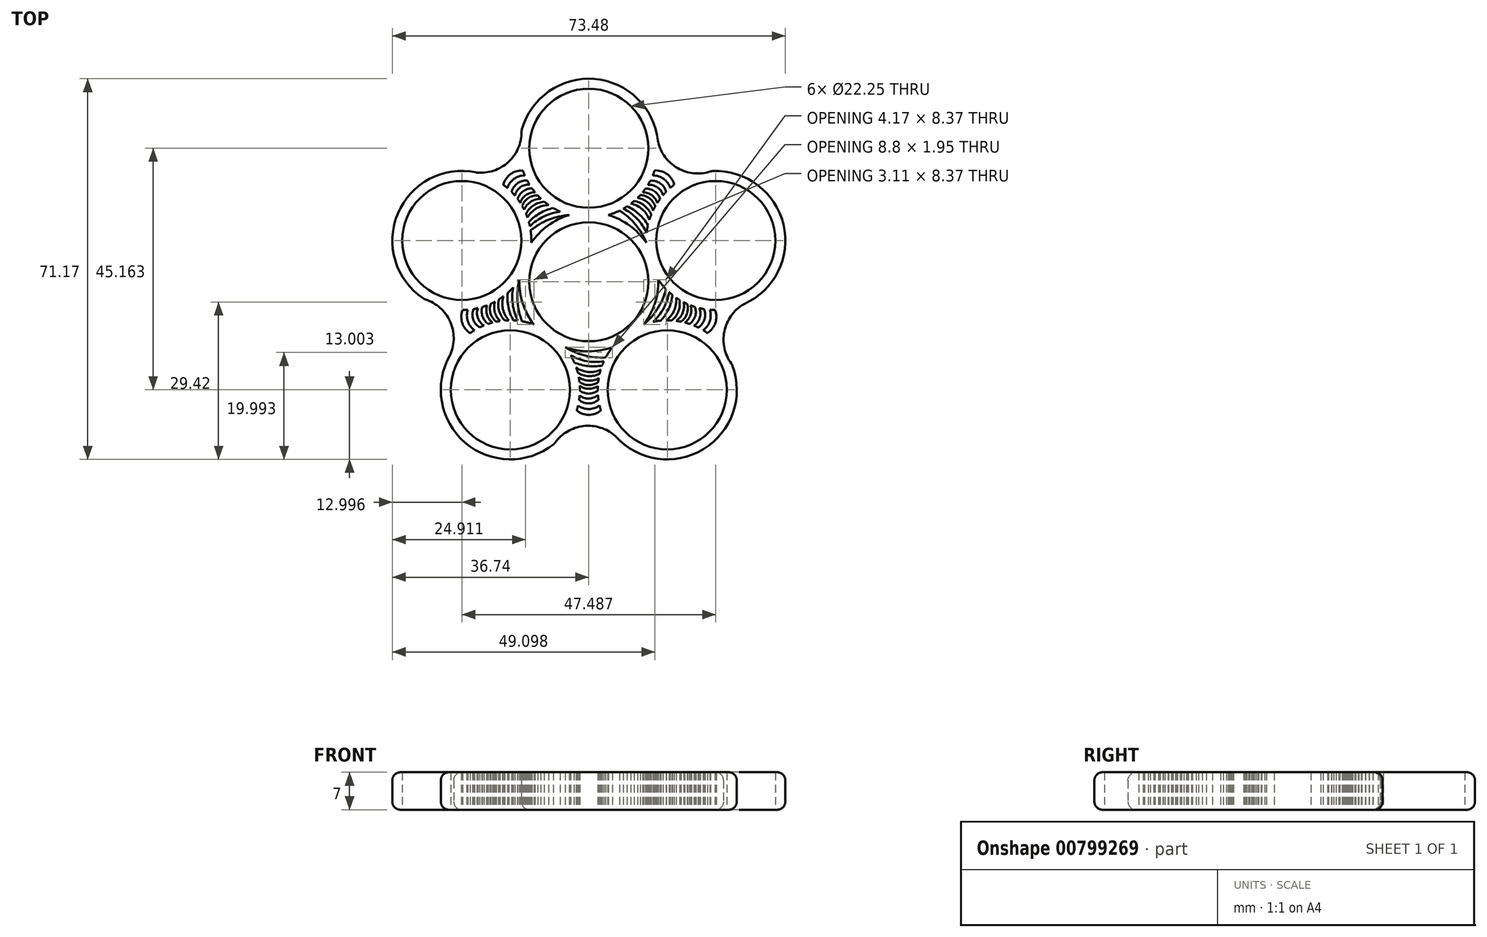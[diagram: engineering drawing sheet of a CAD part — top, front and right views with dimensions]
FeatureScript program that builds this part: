
annotation { "Feature Type Name" : "Feature", "Feature Type Description" : "" }
export const myFeature = defineFeature(function(context is Context, id is Id, definition is map)
    precondition{}
    {
        {
            var Q0;
            Q0=qCreatedBy(makeId("Top.planeOp"),FACE);
            var sketch = newSketch(context, id + "F0", { "sketchPlane" : qUnion([Q0])});
            skCircle(sketch, "E0", {"center": v(0, 0) * mm, "radius": 11.12 * mm});
            skCircle(sketch, "E1", {"center": v(0, 0) * mm, "radius": 13 * mm});
            skCircle(sketch, "E2", {"center": v(0, 24.97) * mm, "radius": 11.12 * mm});
            skCircle(sketch, "E3", {"center": v(0, 24.97) * mm, "radius": 13 * mm});
            skCircle(sketch, "E4.1.0", {"center": v(-23.74, 7.71) * mm, "radius": 11.12 * mm});
            skCircle(sketch, "E4.1.1", {"center": v(-23.74, 7.71) * mm, "radius": 13 * mm});
            skCircle(sketch, "E4.2.0", {"center": v(-14.67, -20.2) * mm, "radius": 11.12 * mm});
            skCircle(sketch, "E4.2.1", {"center": v(-14.67, -20.2) * mm, "radius": 13 * mm});
            skCircle(sketch, "E4.3.0", {"center": v(14.67, -20.2) * mm, "radius": 11.12 * mm});
            skCircle(sketch, "E4.3.1", {"center": v(14.67, -20.2) * mm, "radius": 13 * mm});
            skCircle(sketch, "E4.4.0", {"center": v(23.74, 7.71) * mm, "radius": 11.12 * mm});
            skCircle(sketch, "E4.4.1", {"center": v(23.74, 7.71) * mm, "radius": 13 * mm});
            skArc(sketch, "E5", {"start": v(-20.98, 20.42) * mm, "mid": v(-15.02, 22.43) * mm, "end": v(-12.58, 28.24) * mm});
            skArc(sketch, "E6.1.0", {"start": v(-25.9, -13.65) * mm, "mid": v(-25.97, -7.35) * mm, "end": v(-30.74, -3.24) * mm});
            skArc(sketch, "E6.2.0", {"start": v(4.98, -28.85) * mm, "mid": v(-1.04, -26.97) * mm, "end": v(-6.42, -30.24) * mm});
            skArc(sketch, "E6.3.0", {"start": v(28.98, -4.18) * mm, "mid": v(25.33, -9.32) * mm, "end": v(26.78, -15.45) * mm});
            skArc(sketch, "E6.4.0", {"start": v(12.93, 26.27) * mm, "mid": v(16.7, 21.21) * mm, "end": v(22.97, 20.7) * mm});
            skArc(sketch, "E7", {"start": v(15.97, 18.14) * mm, "mid": v(14.63, 20.14) * mm, "end": v(12.32, 20.81) * mm});
            skArc(sketch, "E8", {"start": v(15.22, 17.53) * mm, "mid": v(13.99, 19.25) * mm, "end": v(11.97, 19.89) * mm});
            skArc(sketch, "E9", {"start": v(14.44, 16.8) * mm, "mid": v(13.36, 18.4) * mm, "end": v(11.5, 18.9) * mm});
            skArc(sketch, "E10", {"start": v(13.88, 16.18) * mm, "mid": v(12.82, 17.66) * mm, "end": v(11.06, 18.14) * mm});
            skArc(sketch, "E11", {"start": v(13.33, 15.5) * mm, "mid": v(12.29, 16.92) * mm, "end": v(10.6, 17.44) * mm});
            skArc(sketch, "E12", {"start": v(12.8, 14.73) * mm, "mid": v(11.77, 16.19) * mm, "end": v(10.07, 16.75) * mm});
            skArc(sketch, "E13", {"start": v(12.42, 14.1) * mm, "mid": v(11.36, 15.6) * mm, "end": v(9.63, 16.23) * mm});
            skArc(sketch, "E14", {"start": v(12.01, 13.32) * mm, "mid": v(10.9, 14.93) * mm, "end": v(9.1, 15.68) * mm});
            skArc(sketch, "E15", {"start": v(11.67, 12.54) * mm, "mid": v(10.4, 14.24) * mm, "end": v(8.46, 15.1) * mm});
            skArc(sketch, "E16", {"start": v(11.33, 11.57) * mm, "mid": v(10, 13.56) * mm, "end": v(7.87, 14.62) * mm});
            skArc(sketch, "E17", {"start": v(11.06, 10.58) * mm, "mid": v(9.39, 12.65) * mm, "end": v(7.17, 14.12) * mm});
            skArc(sketch, "E18", {"start": v(10.82, 9.14) * mm, "mid": v(9.02, 11.78) * mm, "end": v(6.47, 13.69) * mm});
            skArc(sketch, "E19", {"start": v(10.75, 7.31) * mm, "mid": v(8.73, 10.7) * mm, "end": v(5.76, 13.31) * mm});
            skArc(sketch, "E20.1.0", {"start": v(-12.31, 20.8) * mm, "mid": v(-14.63, 20.14) * mm, "end": v(-15.99, 18.15) * mm});
            skArc(sketch, "E20.1.1", {"start": v(-11.97, 19.9) * mm, "mid": v(-13.99, 19.25) * mm, "end": v(-15.22, 17.53) * mm});
            skArc(sketch, "E20.1.2", {"start": v(-11.51, 18.93) * mm, "mid": v(-13.37, 18.4) * mm, "end": v(-14.42, 16.78) * mm});
            skArc(sketch, "E20.1.3", {"start": v(-11.1, 18.2) * mm, "mid": v(-12.84, 17.65) * mm, "end": v(-13.83, 16.12) * mm});
            skArc(sketch, "E20.1.4", {"start": v(-10.62, 17.47) * mm, "mid": v(-12.3, 16.91) * mm, "end": v(-13.31, 15.47) * mm});
            skArc(sketch, "E20.1.5", {"start": v(-10.05, 16.72) * mm, "mid": v(-11.76, 16.2) * mm, "end": v(-12.81, 14.75) * mm});
            skArc(sketch, "E20.1.6", {"start": v(-9.58, 16.18) * mm, "mid": v(-11.33, 15.63) * mm, "end": v(-12.46, 14.17) * mm});
            skArc(sketch, "E20.1.7", {"start": v(-8.95, 15.54) * mm, "mid": v(-10.83, 14.98) * mm, "end": v(-12.1, 13.5) * mm});
            skArc(sketch, "E20.1.8", {"start": v(-8.32, 14.98) * mm, "mid": v(-10.33, 14.3) * mm, "end": v(-11.74, 12.7) * mm});
            skArc(sketch, "E20.1.9", {"start": v(-7.5, 14.35) * mm, "mid": v(-9.8, 13.7) * mm, "end": v(-11.47, 12) * mm});
            skArc(sketch, "E20.1.10", {"start": v(-6.65, 13.8) * mm, "mid": v(-9.13, 12.84) * mm, "end": v(-11.22, 11.19) * mm});
            skArc(sketch, "E20.1.11", {"start": v(-5.35, 13.12) * mm, "mid": v(-8.41, 12.22) * mm, "end": v(-11.02, 10.38) * mm});
            skArc(sketch, "E20.1.12", {"start": v(-3.63, 12.48) * mm, "mid": v(-7.48, 11.61) * mm, "end": v(-10.88, 9.6) * mm});
            skArc(sketch, "E20.2.0", {"start": v(-23.58, -5.28) * mm, "mid": v(-23.67, -7.7) * mm, "end": v(-22.2, -9.6) * mm});
            skArc(sketch, "E20.2.1", {"start": v(-22.62, -5.24) * mm, "mid": v(-22.63, -7.35) * mm, "end": v(-21.37, -9.06) * mm});
            skArc(sketch, "E20.2.2", {"start": v(-21.56, -5.1) * mm, "mid": v(-21.63, -7.03) * mm, "end": v(-20.41, -8.53) * mm});
            skArc(sketch, "E20.2.3", {"start": v(-20.74, -4.93) * mm, "mid": v(-20.75, -6.75) * mm, "end": v(-19.6, -8.17) * mm});
            skArc(sketch, "E20.2.4", {"start": v(-19.9, -4.7) * mm, "mid": v(-19.88, -6.47) * mm, "end": v(-18.83, -7.88) * mm});
            skArc(sketch, "E20.2.5", {"start": v(-19, -4.4) * mm, "mid": v(-19.04, -6.18) * mm, "end": v(-18, -7.63) * mm});
            skArc(sketch, "E20.2.6", {"start": v(-18.34, -4.11) * mm, "mid": v(-18.36, -5.95) * mm, "end": v(-17.33, -7.47) * mm});
            skArc(sketch, "E20.2.7", {"start": v(-17.55, -3.71) * mm, "mid": v(-17.6, -5.67) * mm, "end": v(-16.58, -7.34) * mm});
            skArc(sketch, "E20.2.8", {"start": v(-16.81, -3.28) * mm, "mid": v(-16.79, -5.4) * mm, "end": v(-15.71, -7.24) * mm});
            skArc(sketch, "E20.2.9", {"start": v(-15.96, -2.7) * mm, "mid": v(-16.06, -5.08) * mm, "end": v(-14.96, -7.2) * mm});
            skArc(sketch, "E20.2.10", {"start": v(-15.17, -2.06) * mm, "mid": v(-15.03, -4.72) * mm, "end": v(-14.1, -7.21) * mm});
            skArc(sketch, "E20.2.11", {"start": v(-14.13, -1.03) * mm, "mid": v(-14.22, -4.22) * mm, "end": v(-13.28, -7.27) * mm});
            skArc(sketch, "E20.2.12", {"start": v(-13, 0.4) * mm, "mid": v(-13.36, -3.53) * mm, "end": v(-12.49, -7.38) * mm});
            skArc(sketch, "E20.3.0", {"start": v(-2.26, -24.06) * mm, "mid": v(0, -24.9) * mm, "end": v(2.27, -24.08) * mm});
            skArc(sketch, "E20.3.1", {"start": v(-2.01, -23.13) * mm, "mid": v(0, -23.8) * mm, "end": v(2, -23.12) * mm});
            skArc(sketch, "E20.3.2", {"start": v(-1.81, -22.08) * mm, "mid": v(0, -22.74) * mm, "end": v(1.8, -22.05) * mm});
            skArc(sketch, "E20.3.3", {"start": v(-1.72, -21.25) * mm, "mid": v(0.01, -21.83) * mm, "end": v(1.71, -21.17) * mm});
            skArc(sketch, "E20.3.4", {"start": v(-1.68, -20.38) * mm, "mid": v(0, -20.9) * mm, "end": v(1.68, -20.34) * mm});
            skArc(sketch, "E20.3.5", {"start": v(-1.7, -19.44) * mm, "mid": v(0, -20.02) * mm, "end": v(1.7, -19.47) * mm});
            skArc(sketch, "E20.3.6", {"start": v(-1.76, -18.72) * mm, "mid": v(-0.02, -19.3) * mm, "end": v(1.75, -18.79) * mm});
            skArc(sketch, "E20.3.7", {"start": v(-1.9, -17.84) * mm, "mid": v(-0.05, -18.49) * mm, "end": v(1.86, -18.03) * mm});
            skArc(sketch, "E20.3.8", {"start": v(-2.07, -17) * mm, "mid": v(-0.04, -17.64) * mm, "end": v(2.03, -17.18) * mm});
            skArc(sketch, "E20.3.9", {"start": v(-2.37, -16.02) * mm, "mid": v(-0.13, -16.85) * mm, "end": v(2.23, -16.45) * mm});
            skArc(sketch, "E20.3.10", {"start": v(-2.73, -15.07) * mm, "mid": v(-0.16, -15.75) * mm, "end": v(2.5, -15.64) * mm});
            skArc(sketch, "E20.3.11", {"start": v(-3.38, -13.75) * mm, "mid": v(-0.38, -14.83) * mm, "end": v(2.81, -14.88) * mm});
            skArc(sketch, "E20.3.12", {"start": v(-4.4, -12.23) * mm, "mid": v(-0.77, -13.8) * mm, "end": v(3.16, -14.16) * mm});
            skArc(sketch, "E20.4.0", {"start": v(22.18, -9.59) * mm, "mid": v(23.67, -7.7) * mm, "end": v(23.6, -5.28) * mm});
            skArc(sketch, "E20.4.1", {"start": v(21.38, -9.06) * mm, "mid": v(22.63, -7.35) * mm, "end": v(22.61, -5.24) * mm});
            skArc(sketch, "E20.4.2", {"start": v(20.44, -8.55) * mm, "mid": v(21.63, -7.02) * mm, "end": v(21.53, -5.1) * mm});
            skArc(sketch, "E20.4.3", {"start": v(19.68, -8.2) * mm, "mid": v(20.76, -6.73) * mm, "end": v(20.67, -4.92) * mm});
            skArc(sketch, "E20.4.4", {"start": v(18.86, -7.89) * mm, "mid": v(19.89, -6.46) * mm, "end": v(19.86, -4.7) * mm});
            skArc(sketch, "E20.4.5", {"start": v(17.96, -7.62) * mm, "mid": v(19.03, -6.2) * mm, "end": v(19.04, -4.4) * mm});
            skArc(sketch, "E20.4.6", {"start": v(17.26, -7.46) * mm, "mid": v(18.35, -5.98) * mm, "end": v(18.41, -4.14) * mm});
            skArc(sketch, "E20.4.7", {"start": v(16.38, -7.3) * mm, "mid": v(17.57, -5.76) * mm, "end": v(17.73, -3.8) * mm});
            skArc(sketch, "E20.4.8", {"start": v(15.53, -7.23) * mm, "mid": v(16.76, -5.5) * mm, "end": v(16.97, -3.38) * mm});
            skArc(sketch, "E20.4.9", {"start": v(14.5, -7.2) * mm, "mid": v(15.98, -5.33) * mm, "end": v(16.33, -2.97) * mm});
            skArc(sketch, "E20.4.10", {"start": v(13.49, -7.25) * mm, "mid": v(14.93, -5.02) * mm, "end": v(15.65, -2.46) * mm});
            skArc(sketch, "E20.4.11", {"start": v(12.04, -7.47) * mm, "mid": v(13.99, -4.94) * mm, "end": v(15.02, -1.92) * mm});
            skArc(sketch, "E20.4.12", {"start": v(10.27, -7.96) * mm, "mid": v(12.88, -5) * mm, "end": v(14.44, -1.37) * mm});
            skSolve(sketch);
        }
        {
            var Q0;
            {var subQ0=sQuery(id+"F0.wireOp",EDGE,"E3");var subQ1=sQuery(id+"F0.wireOp",EDGE,"E1");var subQ2=makeQuery(id+"F0.imprint","INTERSECT",VERTEX,{"disambiguationData":[OD(1.0)],"derivedFrom":[subQ1,subQ0]});Q0=makeQuery(id+"F0.imprint","IMPRINT",FACE,{"disambiguationData":[TD([[makeQuery(id+"F0.imprint","IMPRINT",EDGE,{"disambiguationData":[TD([[subQ2,-1.0]])],"derivedFrom":subQ1}),-1.0]])]});}
            var Q1;
            Q1=makeQuery(id+"F0.imprint","IMPRINT",FACE,{"disambiguationData":[TD([[makeQuery(id+"F0.imprint","IMPRINT",EDGE,{"derivedFrom":sQuery(id+"F0.wireOp",EDGE,"E4.1.0")}),-1.0]])]});
            var Q2;
            Q2=makeQuery(id+"F0.imprint","IMPRINT",FACE,{"disambiguationData":[TD([[makeQuery(id+"F0.imprint","IMPRINT",EDGE,{"derivedFrom":sQuery(id+"F0.wireOp",EDGE,"E2")}),-1.0]])]});
            var Q3;
            {var subQ0=sQuery(id+"F0.wireOp",EDGE,"E3");var subQ1=sQuery(id+"F0.wireOp",EDGE,"E1");var subQ2=makeQuery(id+"F0.imprint","INTERSECT",VERTEX,{"disambiguationData":[OD(0.0)],"derivedFrom":[subQ1,subQ0]});Q3=makeQuery(id+"F0.imprint","IMPRINT",FACE,{"disambiguationData":[TD([[makeQuery(id+"F0.imprint","IMPRINT",EDGE,{"disambiguationData":[TD([[subQ2,-1.0]])],"derivedFrom":subQ1}),1.0]])]});}
            var Q4;
            Q4=makeQuery(id+"F0.imprint","IMPRINT",FACE,{"disambiguationData":[TD([[makeQuery(id+"F0.imprint","IMPRINT",EDGE,{"derivedFrom":sQuery(id+"F0.wireOp",EDGE,"E0")}),-1.0]])]});
            var Q5;
            {var subQ0=sQuery(id+"F0.wireOp",EDGE,"E4.2.1");var subQ1=sQuery(id+"F0.wireOp",EDGE,"E1");var subQ2=makeQuery(id+"F0.imprint","INTERSECT",VERTEX,{"disambiguationData":[OD(0.0)],"derivedFrom":[subQ1,subQ0]});Q5=makeQuery(id+"F0.imprint","IMPRINT",FACE,{"disambiguationData":[TD([[makeQuery(id+"F0.imprint","IMPRINT",EDGE,{"disambiguationData":[TD([[subQ2,-1.0]])],"derivedFrom":subQ1}),1.0]])]});}
            var Q6;
            {var subQ0=sQuery(id+"F0.wireOp",EDGE,"E4.1.1");var subQ1=sQuery(id+"F0.wireOp",EDGE,"E1");var subQ2=makeQuery(id+"F0.imprint","INTERSECT",VERTEX,{"disambiguationData":[OD(0.0)],"derivedFrom":[subQ1,subQ0]});Q6=makeQuery(id+"F0.imprint","IMPRINT",FACE,{"disambiguationData":[TD([[makeQuery(id+"F0.imprint","IMPRINT",EDGE,{"disambiguationData":[TD([[subQ2,-1.0]])],"derivedFrom":subQ1}),1.0]])]});}
            var Q7;
            {var subQ0=sQuery(id+"F0.wireOp",EDGE,"E4.4.1");var subQ1=sQuery(id+"F0.wireOp",EDGE,"E1");var subQ2=makeQuery(id+"F0.imprint","INTERSECT",VERTEX,{"disambiguationData":[OD(0.0)],"derivedFrom":[subQ1,subQ0]});Q7=makeQuery(id+"F0.imprint","IMPRINT",FACE,{"disambiguationData":[TD([[makeQuery(id+"F0.imprint","IMPRINT",EDGE,{"disambiguationData":[TD([[subQ2,1.0]])],"derivedFrom":subQ1}),1.0]])]});}
            var Q8;
            {var subQ0=sQuery(id+"F0.wireOp",EDGE,"E4.3.1");var subQ1=sQuery(id+"F0.wireOp",EDGE,"E1");var subQ2=makeQuery(id+"F0.imprint","INTERSECT",VERTEX,{"disambiguationData":[OD(0.0)],"derivedFrom":[subQ1,subQ0]});Q8=makeQuery(id+"F0.imprint","IMPRINT",FACE,{"disambiguationData":[TD([[makeQuery(id+"F0.imprint","IMPRINT",EDGE,{"disambiguationData":[TD([[subQ2,-1.0]])],"derivedFrom":subQ1}),1.0]])]});}
            var Q9;
            {var subQ0=sQuery(id+"F0.wireOp",EDGE,"E4.4.1");var subQ1=sQuery(id+"F0.wireOp",EDGE,"E1");var subQ2=makeQuery(id+"F0.imprint","INTERSECT",VERTEX,{"disambiguationData":[OD(0.0)],"derivedFrom":[subQ1,subQ0]});Q9=makeQuery(id+"F0.imprint","IMPRINT",FACE,{"disambiguationData":[TD([[makeQuery(id+"F0.imprint","IMPRINT",EDGE,{"disambiguationData":[TD([[subQ2,-1.0]])],"derivedFrom":subQ1}),-1.0]])]});}
            var Q10;
            Q10=makeQuery(id+"F0.imprint","IMPRINT",FACE,{"disambiguationData":[TD([[makeQuery(id+"F0.imprint","IMPRINT",EDGE,{"derivedFrom":sQuery(id+"F0.wireOp",EDGE,"E4.4.0")}),-1.0]])]});
            var Q11;
            Q11=makeQuery(id+"F0.imprint","IMPRINT",FACE,{"disambiguationData":[TD([[makeQuery(id+"F0.imprint","IMPRINT",EDGE,{"derivedFrom":sQuery(id+"F0.wireOp",EDGE,"E4.3.0")}),-1.0]])]});
            var Q12;
            {var subQ0=sQuery(id+"F0.wireOp",EDGE,"E4.1.1");var subQ1=sQuery(id+"F0.wireOp",EDGE,"E1");var subQ2=makeQuery(id+"F0.imprint","INTERSECT",VERTEX,{"disambiguationData":[OD(1.0)],"derivedFrom":[subQ1,subQ0]});Q12=makeQuery(id+"F0.imprint","IMPRINT",FACE,{"disambiguationData":[TD([[makeQuery(id+"F0.imprint","IMPRINT",EDGE,{"disambiguationData":[TD([[subQ2,-1.0]])],"derivedFrom":subQ1}),-1.0]])]});}
            var Q13;
            Q13=makeQuery(id+"F0.imprint","IMPRINT",FACE,{"disambiguationData":[TD([[makeQuery(id+"F0.imprint","IMPRINT",EDGE,{"derivedFrom":sQuery(id+"F0.wireOp",EDGE,"E4.2.0")}),-1.0]])]});
            var Q14;
            {var subQ0=sQuery(id+"F0.wireOp",EDGE,"E4.2.1");var subQ1=sQuery(id+"F0.wireOp",EDGE,"E1");var subQ2=makeQuery(id+"F0.imprint","INTERSECT",VERTEX,{"disambiguationData":[OD(1.0)],"derivedFrom":[subQ1,subQ0]});Q14=makeQuery(id+"F0.imprint","IMPRINT",FACE,{"disambiguationData":[TD([[makeQuery(id+"F0.imprint","IMPRINT",EDGE,{"disambiguationData":[TD([[subQ2,-1.0]])],"derivedFrom":subQ1}),-1.0]])]});}
            var Q15;
            {var subQ3=sQuery(id+"F0.wireOp",EDGE,"E7");Q15=makeQuery(id+"F0.imprint","IMPRINT",FACE,{"disambiguationData":[TD([[makeQuery(id+"F0.imprint","IMPRINT",EDGE,{"derivedFrom":subQ3}),-1.0]])]});}
            var Q16;
            {var subQ0=sQuery(id+"F0.wireOp",EDGE,"E8");Q16=makeQuery(id+"F0.imprint","IMPRINT",FACE,{"disambiguationData":[TD([[makeQuery(id+"F0.imprint","IMPRINT",EDGE,{"derivedFrom":subQ0}),1.0]])]});}
            var Q17;
            {var subQ0=sQuery(id+"F0.wireOp",EDGE,"E10");Q17=makeQuery(id+"F0.imprint","IMPRINT",FACE,{"disambiguationData":[TD([[makeQuery(id+"F0.imprint","IMPRINT",EDGE,{"derivedFrom":subQ0}),1.0]])]});}
            var Q18;
            {var subQ0=sQuery(id+"F0.wireOp",EDGE,"E12");Q18=makeQuery(id+"F0.imprint","IMPRINT",FACE,{"disambiguationData":[TD([[makeQuery(id+"F0.imprint","IMPRINT",EDGE,{"derivedFrom":subQ0}),1.0]])]});}
            var Q19;
            {var subQ0=sQuery(id+"F0.wireOp",EDGE,"E14");Q19=makeQuery(id+"F0.imprint","IMPRINT",FACE,{"disambiguationData":[TD([[makeQuery(id+"F0.imprint","IMPRINT",EDGE,{"derivedFrom":subQ0}),1.0]])]});}
            var Q20;
            {var subQ0=sQuery(id+"F0.wireOp",EDGE,"E16");Q20=makeQuery(id+"F0.imprint","IMPRINT",FACE,{"disambiguationData":[TD([[makeQuery(id+"F0.imprint","IMPRINT",EDGE,{"derivedFrom":subQ0}),1.0]])]});}
            var Q21;
            {var subQ0=sQuery(id+"F0.wireOp",EDGE,"E18");Q21=makeQuery(id+"F0.imprint","IMPRINT",FACE,{"disambiguationData":[TD([[makeQuery(id+"F0.imprint","IMPRINT",EDGE,{"derivedFrom":subQ0}),1.0]])]});}
            var Q22;
            {var subQ0=sQuery(id+"F0.wireOp",EDGE,"E4.4.1");var subQ1=sQuery(id+"F0.wireOp",EDGE,"E1");var subQ3=makeQuery(id+"F0.imprint","INTERSECT",VERTEX,{"derivedFrom":[subQ1,subQ0]});Q22=makeQuery(id+"F0.imprint","IMPRINT",FACE,{"disambiguationData":[TD([[makeQuery(id+"F0.imprint","IMPRINT",EDGE,{"disambiguationData":[TD([[subQ3,-1.0]])],"derivedFrom":subQ1}),1.0]])]});}
            var Q23;
            {var subQ0=sQuery(id+"F0.wireOp",EDGE,"E20.1.0");Q23=makeQuery(id+"F0.imprint","IMPRINT",FACE,{"disambiguationData":[TD([[makeQuery(id+"F0.imprint","IMPRINT",EDGE,{"derivedFrom":subQ0}),-1.0]])]});}
            var Q24;
            {var subQ0=sQuery(id+"F0.wireOp",EDGE,"E20.4.0");Q24=makeQuery(id+"F0.imprint","IMPRINT",FACE,{"disambiguationData":[TD([[makeQuery(id+"F0.imprint","IMPRINT",EDGE,{"derivedFrom":subQ0}),-1.0]])]});}
            var Q25;
            {var subQ0=sQuery(id+"F0.wireOp",EDGE,"E20.3.0");Q25=makeQuery(id+"F0.imprint","IMPRINT",FACE,{"disambiguationData":[TD([[makeQuery(id+"F0.imprint","IMPRINT",EDGE,{"derivedFrom":subQ0}),-1.0]])]});}
            var Q26;
            {var subQ0=sQuery(id+"F0.wireOp",EDGE,"E20.2.0");Q26=makeQuery(id+"F0.imprint","IMPRINT",FACE,{"disambiguationData":[TD([[makeQuery(id+"F0.imprint","IMPRINT",EDGE,{"derivedFrom":subQ0}),-1.0]])]});}
            var Q27;
            {var subQ0=sQuery(id+"F0.wireOp",EDGE,"E20.1.1");Q27=makeQuery(id+"F0.imprint","IMPRINT",FACE,{"disambiguationData":[TD([[makeQuery(id+"F0.imprint","IMPRINT",EDGE,{"derivedFrom":subQ0}),1.0]])]});}
            var Q28;
            {var subQ0=sQuery(id+"F0.wireOp",EDGE,"E20.1.3");Q28=makeQuery(id+"F0.imprint","IMPRINT",FACE,{"disambiguationData":[TD([[makeQuery(id+"F0.imprint","IMPRINT",EDGE,{"derivedFrom":subQ0}),1.0]])]});}
            var Q29;
            {var subQ0=sQuery(id+"F0.wireOp",EDGE,"E20.1.5");Q29=makeQuery(id+"F0.imprint","IMPRINT",FACE,{"disambiguationData":[TD([[makeQuery(id+"F0.imprint","IMPRINT",EDGE,{"derivedFrom":subQ0}),1.0]])]});}
            var Q30;
            {var subQ0=sQuery(id+"F0.wireOp",EDGE,"E20.1.7");Q30=makeQuery(id+"F0.imprint","IMPRINT",FACE,{"disambiguationData":[TD([[makeQuery(id+"F0.imprint","IMPRINT",EDGE,{"derivedFrom":subQ0}),1.0]])]});}
            var Q31;
            {var subQ0=sQuery(id+"F0.wireOp",EDGE,"E20.1.9");Q31=makeQuery(id+"F0.imprint","IMPRINT",FACE,{"disambiguationData":[TD([[makeQuery(id+"F0.imprint","IMPRINT",EDGE,{"derivedFrom":subQ0}),1.0]])]});}
            var Q32;
            {var subQ0=sQuery(id+"F0.wireOp",EDGE,"E20.1.11");Q32=makeQuery(id+"F0.imprint","IMPRINT",FACE,{"disambiguationData":[TD([[makeQuery(id+"F0.imprint","IMPRINT",EDGE,{"derivedFrom":subQ0}),1.0]])]});}
            var Q33;
            {var subQ0=sQuery(id+"F0.wireOp",EDGE,"E20.4.1");Q33=makeQuery(id+"F0.imprint","IMPRINT",FACE,{"disambiguationData":[TD([[makeQuery(id+"F0.imprint","IMPRINT",EDGE,{"derivedFrom":subQ0}),1.0]])]});}
            var Q34;
            {var subQ0=sQuery(id+"F0.wireOp",EDGE,"E20.4.3");Q34=makeQuery(id+"F0.imprint","IMPRINT",FACE,{"disambiguationData":[TD([[makeQuery(id+"F0.imprint","IMPRINT",EDGE,{"derivedFrom":subQ0}),1.0]])]});}
            var Q35;
            {var subQ0=sQuery(id+"F0.wireOp",EDGE,"E20.4.5");Q35=makeQuery(id+"F0.imprint","IMPRINT",FACE,{"disambiguationData":[TD([[makeQuery(id+"F0.imprint","IMPRINT",EDGE,{"derivedFrom":subQ0}),1.0]])]});}
            var Q36;
            {var subQ0=sQuery(id+"F0.wireOp",EDGE,"E20.4.7");Q36=makeQuery(id+"F0.imprint","IMPRINT",FACE,{"disambiguationData":[TD([[makeQuery(id+"F0.imprint","IMPRINT",EDGE,{"derivedFrom":subQ0}),1.0]])]});}
            var Q37;
            {var subQ0=sQuery(id+"F0.wireOp",EDGE,"E20.4.9");Q37=makeQuery(id+"F0.imprint","IMPRINT",FACE,{"disambiguationData":[TD([[makeQuery(id+"F0.imprint","IMPRINT",EDGE,{"derivedFrom":subQ0}),1.0]])]});}
            var Q38;
            {var subQ0=sQuery(id+"F0.wireOp",EDGE,"E20.4.11");Q38=makeQuery(id+"F0.imprint","IMPRINT",FACE,{"disambiguationData":[TD([[makeQuery(id+"F0.imprint","IMPRINT",EDGE,{"derivedFrom":subQ0}),1.0]])]});}
            var Q39;
            {var subQ0=sQuery(id+"F0.wireOp",EDGE,"E20.3.1");Q39=makeQuery(id+"F0.imprint","IMPRINT",FACE,{"disambiguationData":[TD([[makeQuery(id+"F0.imprint","IMPRINT",EDGE,{"derivedFrom":subQ0}),1.0]])]});}
            var Q40;
            {var subQ0=sQuery(id+"F0.wireOp",EDGE,"E20.3.3");Q40=makeQuery(id+"F0.imprint","IMPRINT",FACE,{"disambiguationData":[TD([[makeQuery(id+"F0.imprint","IMPRINT",EDGE,{"derivedFrom":subQ0}),1.0]])]});}
            var Q41;
            {var subQ0=sQuery(id+"F0.wireOp",EDGE,"E20.3.5");Q41=makeQuery(id+"F0.imprint","IMPRINT",FACE,{"disambiguationData":[TD([[makeQuery(id+"F0.imprint","IMPRINT",EDGE,{"derivedFrom":subQ0}),1.0]])]});}
            var Q42;
            {var subQ0=sQuery(id+"F0.wireOp",EDGE,"E20.3.7");Q42=makeQuery(id+"F0.imprint","IMPRINT",FACE,{"disambiguationData":[TD([[makeQuery(id+"F0.imprint","IMPRINT",EDGE,{"derivedFrom":subQ0}),1.0]])]});}
            var Q43;
            {var subQ0=sQuery(id+"F0.wireOp",EDGE,"E20.3.9");Q43=makeQuery(id+"F0.imprint","IMPRINT",FACE,{"disambiguationData":[TD([[makeQuery(id+"F0.imprint","IMPRINT",EDGE,{"derivedFrom":subQ0}),1.0]])]});}
            var Q44;
            {var subQ0=sQuery(id+"F0.wireOp",EDGE,"E20.3.11");Q44=makeQuery(id+"F0.imprint","IMPRINT",FACE,{"disambiguationData":[TD([[makeQuery(id+"F0.imprint","IMPRINT",EDGE,{"derivedFrom":subQ0}),1.0]])]});}
            var Q45;
            {var subQ0=sQuery(id+"F0.wireOp",EDGE,"E20.2.1");Q45=makeQuery(id+"F0.imprint","IMPRINT",FACE,{"disambiguationData":[TD([[makeQuery(id+"F0.imprint","IMPRINT",EDGE,{"derivedFrom":subQ0}),1.0]])]});}
            var Q46;
            {var subQ0=sQuery(id+"F0.wireOp",EDGE,"E20.2.3");Q46=makeQuery(id+"F0.imprint","IMPRINT",FACE,{"disambiguationData":[TD([[makeQuery(id+"F0.imprint","IMPRINT",EDGE,{"derivedFrom":subQ0}),1.0]])]});}
            var Q47;
            {var subQ0=sQuery(id+"F0.wireOp",EDGE,"E20.2.5");Q47=makeQuery(id+"F0.imprint","IMPRINT",FACE,{"disambiguationData":[TD([[makeQuery(id+"F0.imprint","IMPRINT",EDGE,{"derivedFrom":subQ0}),1.0]])]});}
            var Q48;
            {var subQ0=sQuery(id+"F0.wireOp",EDGE,"E20.2.7");Q48=makeQuery(id+"F0.imprint","IMPRINT",FACE,{"disambiguationData":[TD([[makeQuery(id+"F0.imprint","IMPRINT",EDGE,{"derivedFrom":subQ0}),1.0]])]});}
            var Q49;
            {var subQ0=sQuery(id+"F0.wireOp",EDGE,"E20.2.9");Q49=makeQuery(id+"F0.imprint","IMPRINT",FACE,{"disambiguationData":[TD([[makeQuery(id+"F0.imprint","IMPRINT",EDGE,{"derivedFrom":subQ0}),1.0]])]});}
            var Q50;
            {var subQ0=sQuery(id+"F0.wireOp",EDGE,"E20.2.11");Q50=makeQuery(id+"F0.imprint","IMPRINT",FACE,{"disambiguationData":[TD([[makeQuery(id+"F0.imprint","IMPRINT",EDGE,{"derivedFrom":subQ0}),1.0]])]});}
            extrude(context, id + "F1", {"entities" : qUnion([Q0, Q1, Q2, Q3, Q4, Q5, Q6, Q7, Q8, Q9, Q10, Q11, Q12, Q13, Q14, Q15, Q16, Q17, Q18, Q19, Q20, Q21, Q22, Q23, Q24, Q25, Q26, Q27, Q28, Q29, Q30, Q31, Q32, Q33, Q34, Q35, Q36, Q37, Q38, Q39, Q40, Q41, Q42, Q43, Q44, Q45, Q46, Q47, Q48, Q49, Q50]), "depth" : 7 * mm, "offsetDistance" : 25 * mm});
        }
        {
            var Q0;
            {var subQ0=sQuery(id+"F0.wireOp",EDGE,"E4.3.1");Q0=makeQuery(id+"F1.opExtrude","SWEPT_FACE",FACE,{"disambiguationData":[OSD([subQ0]),TDD([makeQuery(id+"F0.imprint","IMPRINT",EDGE,{"disambiguationData":[TD([[makeQuery(id+"F0.imprint","INTERSECT",VERTEX,{"derivedFrom":[subQ0,sQuery(id+"F0.wireOp",EDGE,"E6.2.0")]}),-1.0]])],"derivedFrom":subQ0})])]});}
            var Q1;
            Q1=makeQuery(id+"F1.opExtrude","SWEPT_FACE",FACE,{"disambiguationData":[OSD([sQuery(id+"F0.wireOp",EDGE,"E6.2.0")])]});
            var Q2;
            {var subQ0=sQuery(id+"F0.wireOp",EDGE,"E4.2.1");Q2=makeQuery(id+"F1.opExtrude","SWEPT_FACE",FACE,{"disambiguationData":[OSD([subQ0]),TDD([makeQuery(id+"F0.imprint","IMPRINT",EDGE,{"disambiguationData":[TD([[makeQuery(id+"F0.imprint","INTERSECT",VERTEX,{"derivedFrom":[subQ0,sQuery(id+"F0.wireOp",EDGE,"E6.1.0")]}),-1.0]])],"derivedFrom":subQ0})])]});}
            var Q3;
            Q3=makeQuery(id+"F1.opExtrude","SWEPT_FACE",FACE,{"disambiguationData":[OSD([sQuery(id+"F0.wireOp",EDGE,"E6.1.0")])]});
            var Q4;
            {var subQ0=sQuery(id+"F0.wireOp",EDGE,"E4.1.1");Q4=makeQuery(id+"F1.opExtrude","SWEPT_FACE",FACE,{"disambiguationData":[OSD([subQ0]),TDD([makeQuery(id+"F0.imprint","IMPRINT",EDGE,{"disambiguationData":[TD([[makeQuery(id+"F0.imprint","INTERSECT",VERTEX,{"derivedFrom":[subQ0,sQuery(id+"F0.wireOp",EDGE,"E5")]}),-1.0]])],"derivedFrom":subQ0})])]});}
            var Q5;
            Q5=makeQuery(id+"F1.opExtrude","SWEPT_FACE",FACE,{"disambiguationData":[OSD([sQuery(id+"F0.wireOp",EDGE,"E5")])]});
            var Q6;
            {var subQ0=sQuery(id+"F0.wireOp",EDGE,"E3");Q6=makeQuery(id+"F1.opExtrude","SWEPT_FACE",FACE,{"disambiguationData":[OSD([subQ0]),TDD([makeQuery(id+"F0.imprint","IMPRINT",EDGE,{"disambiguationData":[TD([[makeQuery(id+"F0.imprint","INTERSECT",VERTEX,{"disambiguationData":[OD(0.0)],"derivedFrom":[subQ0,sQuery(id+"F0.wireOp",EDGE,"E5")]}),1.0]])],"derivedFrom":subQ0})])]});}
            var Q7;
            Q7=makeQuery(id+"F1.opExtrude","SWEPT_FACE",FACE,{"disambiguationData":[OSD([sQuery(id+"F0.wireOp",EDGE,"E6.4.0")])]});
            var Q8;
            {var subQ0=sQuery(id+"F0.wireOp",EDGE,"E4.4.1");Q8=makeQuery(id+"F1.opExtrude","SWEPT_FACE",FACE,{"disambiguationData":[OSD([subQ0]),TDD([makeQuery(id+"F0.imprint","IMPRINT",EDGE,{"disambiguationData":[TD([[makeQuery(id+"F0.imprint","INTERSECT",VERTEX,{"derivedFrom":[subQ0,sQuery(id+"F0.wireOp",EDGE,"E6.3.0")]}),-1.0]])],"derivedFrom":subQ0})])]});}
            var Q9;
            Q9=makeQuery(id+"F1.opExtrude","SWEPT_FACE",FACE,{"disambiguationData":[OSD([sQuery(id+"F0.wireOp",EDGE,"E6.3.0")])]});
            fillet(context, id + "F2", {"entities" : qUnion([Q0, Q1, Q2, Q3, Q4, Q5, Q6, Q7, Q8, Q9]), "radius" : 1.5 * mm, "tangentPropagation" : true, "allowEdgeOverflow" : false});
        }
    });
